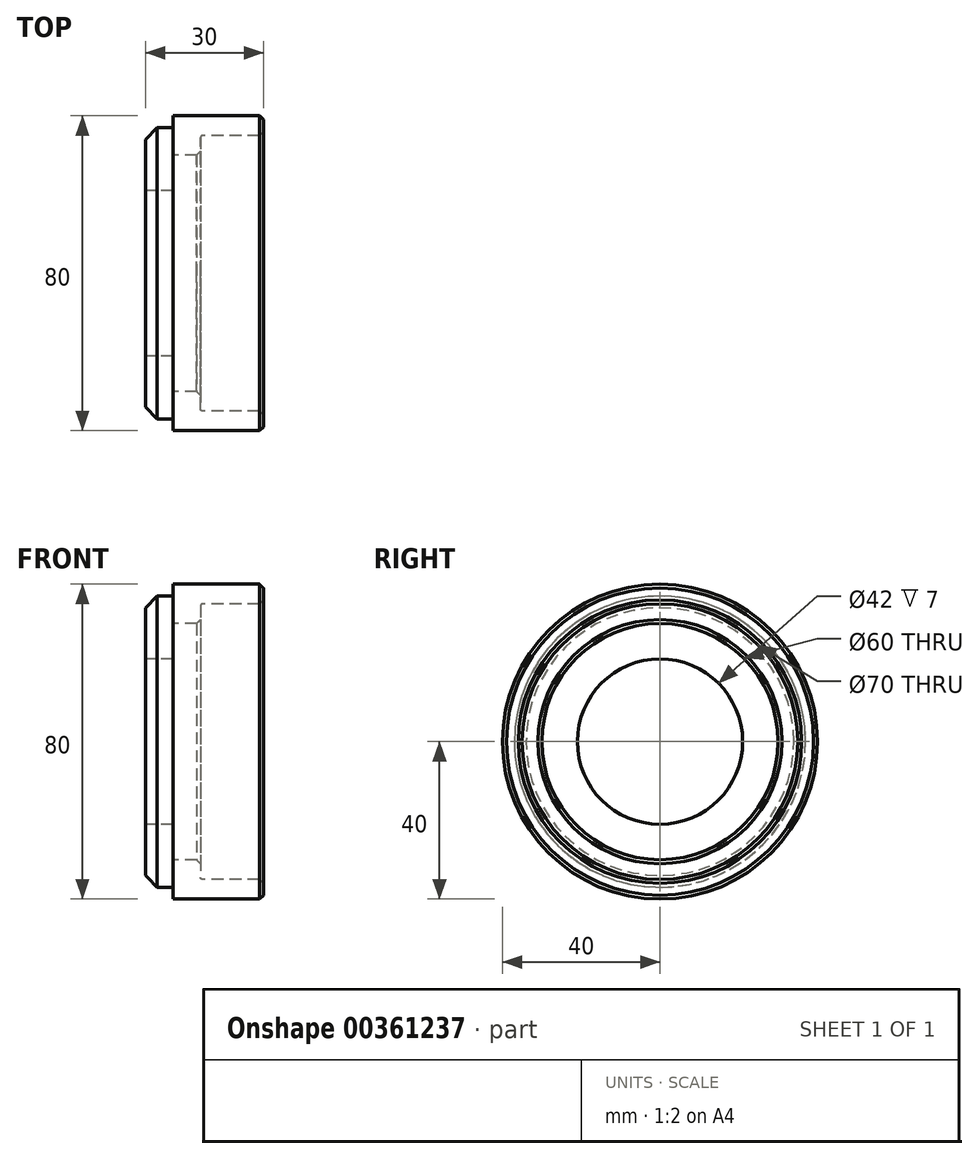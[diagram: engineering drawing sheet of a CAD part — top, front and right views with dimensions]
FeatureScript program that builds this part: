
annotation { "Feature Type Name" : "Feature", "Feature Type Description" : "" }
export const myFeature = defineFeature(function(context is Context, id is Id, definition is map)
    precondition{}
    {
        {
            var Q0;
            Q0=qCreatedBy(makeId("Front.planeOp"),FACE);
            var sketch = newSketch(context, id + "F0", { "sketchPlane" : qUnion([Q0])});
            skLineSegment(sketch, "E0", {"start": v(0, 21) * mm, "end": v(0, 30) * mm});
            skLineSegment(sketch, "E1", {"start": v(0, 30) * mm, "end": v(7, 30) * mm});
            skLineSegment(sketch, "E2", {"start": v(7, 30) * mm, "end": v(7, 35) * mm});
            skLineSegment(sketch, "E3", {"start": v(7, 35) * mm, "end": v(23, 35) * mm});
            skLineSegment(sketch, "E4", {"start": v(23, 35) * mm, "end": v(23, 40) * mm});
            skLineSegment(sketch, "E5", {"start": v(23, 40) * mm, "end": v(0, 40) * mm});
            skLineSegment(sketch, "E6", {"start": v(0, 40) * mm, "end": v(0, 37) * mm});
            skLineSegment(sketch, "E7", {"start": v(0, 37) * mm, "end": v(-7, 37) * mm});
            skLineSegment(sketch, "E8", {"start": v(-7, 37) * mm, "end": v(-7, 21) * mm});
            skLineSegment(sketch, "E9", {"start": v(-7, 0) * mm, "end": v(0, 0) * mm, "construction": true});
            skLineSegment(sketch, "E10", {"start": v(-7, 21) * mm, "end": v(0, 21) * mm});
            skSolve(sketch);
        }
        {
            var Q0;
            Q0 = qSketchRegion(id + "F0", true);
            var Q1;
            Q1=sQuery(id+"F0.wireOp",EDGE,"E9");
            revolve(context, id + "F1", {"entities" : qUnion([Q0]), "axis" : qUnion([Q1]), "revolveType" : RevolveType.FULL});
        }
        {
            var Q0;
            Q0=makeQuery(id+"F1.opRevolve","SWEPT_EDGE",EDGE,{"disambiguationData":[OSD([sQuery(id+"F0.wireOp",EDGE,"E7"),sQuery(id+"F0.wireOp",EDGE,"E8")])]});
            chamfer(context, id + "F2", {"entities" : qUnion([Q0]), "width" : 3 * mm, "tangentPropagation" : true});
        }
        {
            var Q0;
            Q0=makeQuery(id+"F1.opRevolve","SWEPT_EDGE",EDGE,{"disambiguationData":[OSD([sQuery(id+"F0.wireOp",EDGE,"E4"),sQuery(id+"F0.wireOp",EDGE,"E5")])]});
            var Q1;
            Q1=makeQuery(id+"F1.opRevolve","SWEPT_EDGE",EDGE,{"disambiguationData":[OSD([sQuery(id+"F0.wireOp",EDGE,"E3"),sQuery(id+"F0.wireOp",EDGE,"E4")])]});
            var Q2;
            Q2=makeQuery(id+"F1.opRevolve","SWEPT_EDGE",EDGE,{"disambiguationData":[OSD([sQuery(id+"F0.wireOp",EDGE,"E1"),sQuery(id+"F0.wireOp",EDGE,"E2")])]});
            chamfer(context, id + "F3", {"entities" : qUnion([Q0, Q1, Q2]), "width" : 1 * mm, "tangentPropagation" : true});
        }
        {
            var Q0;
            Q0=makeQuery(id+"F1.opRevolve","SWEPT_EDGE",EDGE,{"disambiguationData":[OSD([sQuery(id+"F0.wireOp",EDGE,"E0"),sQuery(id+"F0.wireOp",EDGE,"E1")])]});
            var Q1;
            Q1=makeQuery(id+"F1.opRevolve","SWEPT_EDGE",EDGE,{"disambiguationData":[OSD([sQuery(id+"F0.wireOp",EDGE,"E2"),sQuery(id+"F0.wireOp",EDGE,"E3")])]});
            fillet(context, id + "F4", {"entities" : qUnion([Q0, Q1]), "radius" : 0.5 * mm, "tangentPropagation" : true, "allowEdgeOverflow" : false});
        }
    });
